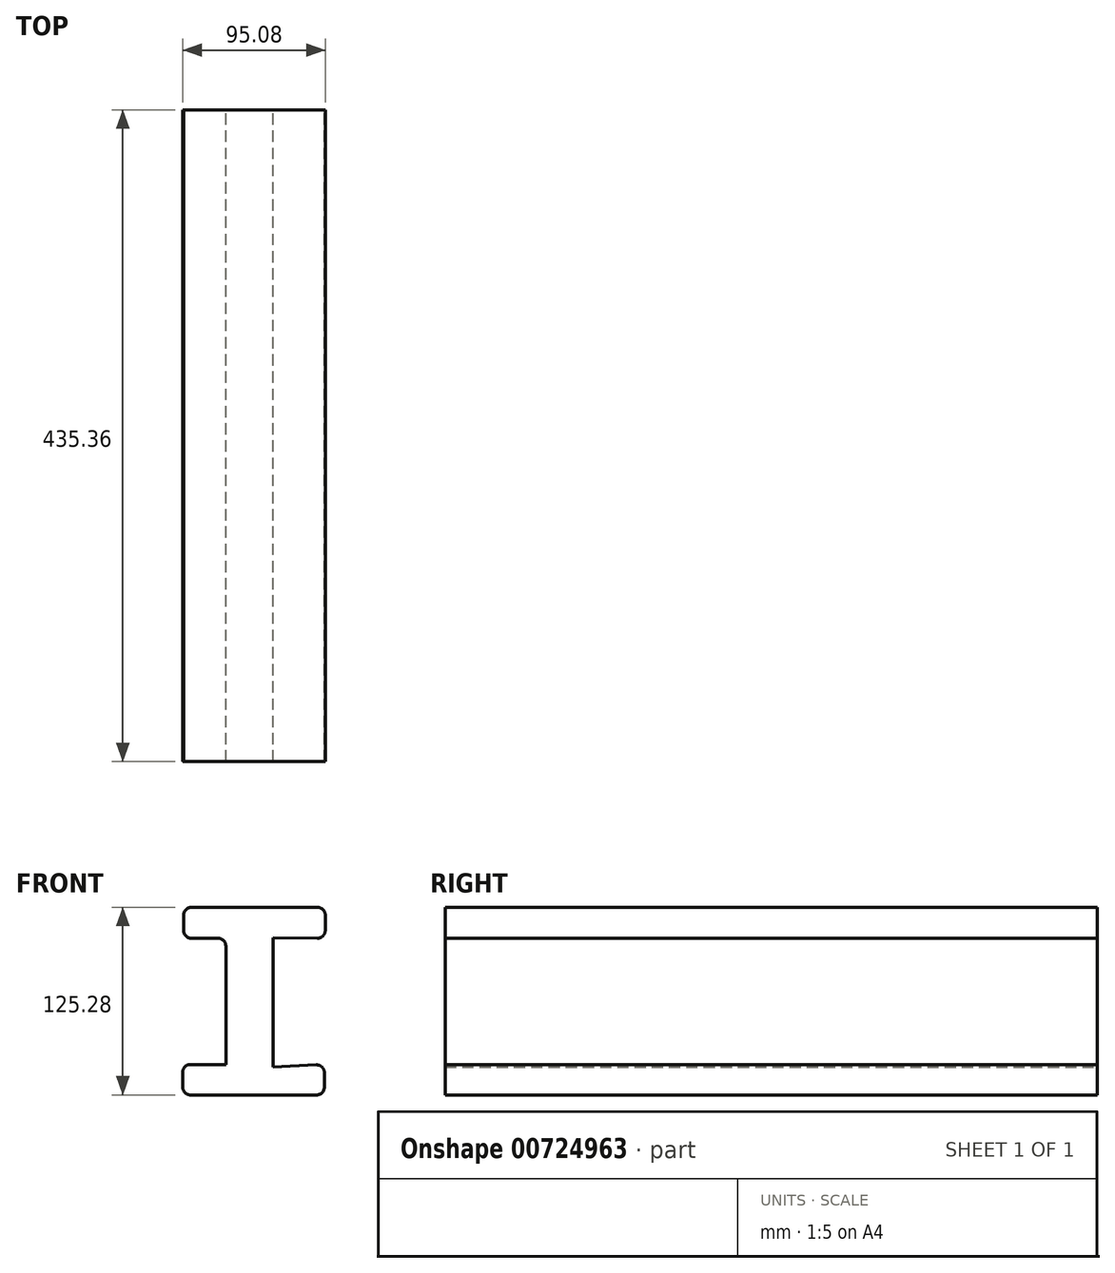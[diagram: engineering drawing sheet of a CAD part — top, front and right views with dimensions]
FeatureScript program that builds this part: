
annotation { "Feature Type Name" : "Feature", "Feature Type Description" : "" }
export const myFeature = defineFeature(function(context is Context, id is Id, definition is map)
    precondition{}
    {
        {
            var Q0;
            Q0=qCreatedBy(makeId("Front.planeOp"),FACE);
            var sketch = newSketch(context, id + "F0", { "sketchPlane" : qUnion([Q0])});
            skLineSegment(sketch, "E0", {"start": v(-18.09, 39.47) * mm, "end": v(-18.09, -44.85) * mm});
            skLineSegment(sketch, "E1", {"start": v(13.6, 39.77) * mm, "end": v(13.6, -46.65) * mm});
            skLineSegment(sketch, "E2", {"start": v(-18.09, 39.47) * mm, "end": v(-46.2, 39.47) * mm});
            skLineSegment(sketch, "E3", {"start": v(-46.2, 39.47) * mm, "end": v(-46.2, 60.1) * mm});
            skLineSegment(sketch, "E4", {"start": v(-46.2, 60.1) * mm, "end": v(48.29, 60.1) * mm});
            skLineSegment(sketch, "E5", {"start": v(48.29, 60.1) * mm, "end": v(48.29, 39.47) * mm});
            skLineSegment(sketch, "E6", {"start": v(48.29, 39.47) * mm, "end": v(13.6, 39.77) * mm});
            skLineSegment(sketch, "E7", {"start": v(-18.09, -44.85) * mm, "end": v(-46.8, -44.85) * mm});
            skLineSegment(sketch, "E8", {"start": v(-46.8, -44.85) * mm, "end": v(-46.8, -65.18) * mm});
            skLineSegment(sketch, "E9", {"start": v(-46.8, -65.18) * mm, "end": v(47.7, -65.18) * mm});
            skLineSegment(sketch, "E10", {"start": v(47.7, -65.18) * mm, "end": v(47.7, -44.85) * mm});
            skLineSegment(sketch, "E11", {"start": v(47.7, -44.85) * mm, "end": v(13.6, -46.65) * mm});
            skSolve(sketch);
        }
        {
            var Q0;
            Q0=makeQuery(id+"F0.imprint","IMPRINT",FACE,{"disambiguationData":[TD([[makeQuery(id+"F0.imprint","IMPRINT",EDGE,{"derivedFrom":sQuery(id+"F0.wireOp",EDGE,"E0")}),1.0]])]});
            extrude(context, id + "F1", {"entities" : qUnion([Q0]), "depth" : 76.2 * mm, "offsetDistance" : 25.4 * mm});
        }
        {
            var Q0;
            Q0=makeQuery(id+"F1.opExtrude","CAP_FACE",FACE,{"disambiguationData":[OSD([sQuery(id+"F0.wireOp",EDGE,"E0"),sQuery(id+"F0.wireOp",EDGE,"E1"),sQuery(id+"F0.wireOp",EDGE,"E2"),sQuery(id+"F0.wireOp",EDGE,"E3"),sQuery(id+"F0.wireOp",EDGE,"E4"),sQuery(id+"F0.wireOp",EDGE,"E5"),sQuery(id+"F0.wireOp",EDGE,"E6"),sQuery(id+"F0.wireOp",EDGE,"E7"),sQuery(id+"F0.wireOp",EDGE,"E8"),sQuery(id+"F0.wireOp",EDGE,"E9"),sQuery(id+"F0.wireOp",EDGE,"E10"),sQuery(id+"F0.wireOp",EDGE,"E11")])],"isStart":true});
            extrude(context, id + "F2", {"entities" : qUnion([Q0]), "operationType" : NewBodyOperationType.ADD, "depth" : 150.11 * mm, "offsetDistance" : 25.4 * mm});
        }
        {
            var Q0;
            Q0=makeQuery(id+"F2.opExtrude","CAP_FACE",FACE,{"disambiguationData":[OSD([sQuery(id+"F0.wireOp",EDGE,"E0"),sQuery(id+"F0.wireOp",EDGE,"E1"),sQuery(id+"F0.wireOp",EDGE,"E2"),sQuery(id+"F0.wireOp",EDGE,"E3"),sQuery(id+"F0.wireOp",EDGE,"E4"),sQuery(id+"F0.wireOp",EDGE,"E5"),sQuery(id+"F0.wireOp",EDGE,"E6"),sQuery(id+"F0.wireOp",EDGE,"E7"),sQuery(id+"F0.wireOp",EDGE,"E8"),sQuery(id+"F0.wireOp",EDGE,"E9"),sQuery(id+"F0.wireOp",EDGE,"E10"),sQuery(id+"F0.wireOp",EDGE,"E11")])],"isStart":false});
            extrude(context, id + "F3", {"entities" : qUnion([Q0]), "operationType" : NewBodyOperationType.ADD, "depth" : 209.04 * mm, "offsetDistance" : 25.4 * mm});
        }
        {
            var Q0;
            {var subQ0=sQuery(id+"F0.wireOp",EDGE,"E3");var subQ1=sQuery(id+"F0.wireOp",EDGE,"E2");Q0=makeQuery(id+"F3.boolean.opBoolean","MERGE",EDGE,{"derivedFrom":[makeQuery(id+"F2.boolean.opBoolean","MERGE",EDGE,{"derivedFrom":[makeQuery(id+"F1.opExtrude","SWEPT_EDGE",EDGE,{"disambiguationData":[OSD([subQ1,subQ0])]}),makeQuery(id+"F2.opExtrude","SWEPT_EDGE",EDGE,{"disambiguationData":[OSD([subQ1,subQ0])]})]}),makeQuery(id+"F3.opExtrude","SWEPT_EDGE",EDGE,{"disambiguationData":[OSD([subQ1,subQ0])]})]});}
            var Q1;
            {var subQ0=sQuery(id+"F0.wireOp",EDGE,"E2");var subQ1=sQuery(id+"F0.wireOp",EDGE,"E0");Q1=makeQuery(id+"F3.boolean.opBoolean","MERGE",EDGE,{"derivedFrom":[makeQuery(id+"F2.boolean.opBoolean","MERGE",EDGE,{"derivedFrom":[makeQuery(id+"F1.opExtrude","SWEPT_EDGE",EDGE,{"disambiguationData":[OSD([subQ1,subQ0])]}),makeQuery(id+"F2.opExtrude","SWEPT_EDGE",EDGE,{"disambiguationData":[OSD([subQ1,subQ0])]})]}),makeQuery(id+"F3.opExtrude","SWEPT_EDGE",EDGE,{"disambiguationData":[OSD([subQ1,subQ0])]})]});}
            var Q2;
            {var subQ0=sQuery(id+"F0.wireOp",EDGE,"E8");var subQ1=sQuery(id+"F0.wireOp",EDGE,"E7");Q2=makeQuery(id+"F3.boolean.opBoolean","MERGE",EDGE,{"derivedFrom":[makeQuery(id+"F2.boolean.opBoolean","MERGE",EDGE,{"derivedFrom":[makeQuery(id+"F1.opExtrude","SWEPT_EDGE",EDGE,{"disambiguationData":[OSD([subQ1,subQ0])]}),makeQuery(id+"F2.opExtrude","SWEPT_EDGE",EDGE,{"disambiguationData":[OSD([subQ1,subQ0])]})]}),makeQuery(id+"F3.opExtrude","SWEPT_EDGE",EDGE,{"disambiguationData":[OSD([subQ1,subQ0])]})]});}
            var Q3;
            {var subQ0=sQuery(id+"F0.wireOp",EDGE,"E9");var subQ1=sQuery(id+"F0.wireOp",EDGE,"E8");Q3=makeQuery(id+"F3.boolean.opBoolean","MERGE",EDGE,{"derivedFrom":[makeQuery(id+"F2.boolean.opBoolean","MERGE",EDGE,{"derivedFrom":[makeQuery(id+"F1.opExtrude","SWEPT_EDGE",EDGE,{"disambiguationData":[OSD([subQ1,subQ0])]}),makeQuery(id+"F2.opExtrude","SWEPT_EDGE",EDGE,{"disambiguationData":[OSD([subQ1,subQ0])]})]}),makeQuery(id+"F3.opExtrude","SWEPT_EDGE",EDGE,{"disambiguationData":[OSD([subQ1,subQ0])]})]});}
            var Q4;
            {var subQ0=sQuery(id+"F0.wireOp",EDGE,"E10");var subQ1=sQuery(id+"F0.wireOp",EDGE,"E9");Q4=makeQuery(id+"F3.boolean.opBoolean","MERGE",EDGE,{"derivedFrom":[makeQuery(id+"F2.boolean.opBoolean","MERGE",EDGE,{"derivedFrom":[makeQuery(id+"F1.opExtrude","SWEPT_EDGE",EDGE,{"disambiguationData":[OSD([subQ1,subQ0])]}),makeQuery(id+"F2.opExtrude","SWEPT_EDGE",EDGE,{"disambiguationData":[OSD([subQ1,subQ0])]})]}),makeQuery(id+"F3.opExtrude","SWEPT_EDGE",EDGE,{"disambiguationData":[OSD([subQ1,subQ0])]})]});}
            var Q5;
            {var subQ0=sQuery(id+"F0.wireOp",EDGE,"E11");var subQ1=sQuery(id+"F0.wireOp",EDGE,"E10");Q5=makeQuery(id+"F3.boolean.opBoolean","MERGE",EDGE,{"derivedFrom":[makeQuery(id+"F2.boolean.opBoolean","MERGE",EDGE,{"derivedFrom":[makeQuery(id+"F1.opExtrude","SWEPT_EDGE",EDGE,{"disambiguationData":[OSD([subQ1,subQ0])]}),makeQuery(id+"F2.opExtrude","SWEPT_EDGE",EDGE,{"disambiguationData":[OSD([subQ1,subQ0])]})]}),makeQuery(id+"F3.opExtrude","SWEPT_EDGE",EDGE,{"disambiguationData":[OSD([subQ1,subQ0])]})]});}
            var Q6;
            {var subQ0=sQuery(id+"F0.wireOp",EDGE,"E6");var subQ1=sQuery(id+"F0.wireOp",EDGE,"E5");Q6=makeQuery(id+"F3.boolean.opBoolean","MERGE",EDGE,{"derivedFrom":[makeQuery(id+"F2.boolean.opBoolean","MERGE",EDGE,{"derivedFrom":[makeQuery(id+"F1.opExtrude","SWEPT_EDGE",EDGE,{"disambiguationData":[OSD([subQ1,subQ0])]}),makeQuery(id+"F2.opExtrude","SWEPT_EDGE",EDGE,{"disambiguationData":[OSD([subQ1,subQ0])]})]}),makeQuery(id+"F3.opExtrude","SWEPT_EDGE",EDGE,{"disambiguationData":[OSD([subQ1,subQ0])]})]});}
            var Q7;
            {var subQ0=sQuery(id+"F0.wireOp",EDGE,"E5");var subQ1=sQuery(id+"F0.wireOp",EDGE,"E4");Q7=makeQuery(id+"F3.boolean.opBoolean","MERGE",EDGE,{"derivedFrom":[makeQuery(id+"F2.boolean.opBoolean","MERGE",EDGE,{"derivedFrom":[makeQuery(id+"F1.opExtrude","SWEPT_EDGE",EDGE,{"disambiguationData":[OSD([subQ1,subQ0])]}),makeQuery(id+"F2.opExtrude","SWEPT_EDGE",EDGE,{"disambiguationData":[OSD([subQ1,subQ0])]})]}),makeQuery(id+"F3.opExtrude","SWEPT_EDGE",EDGE,{"disambiguationData":[OSD([subQ1,subQ0])]})]});}
            var Q8;
            {var subQ0=sQuery(id+"F0.wireOp",EDGE,"E4");var subQ1=sQuery(id+"F0.wireOp",EDGE,"E3");Q8=makeQuery(id+"F3.boolean.opBoolean","MERGE",EDGE,{"derivedFrom":[makeQuery(id+"F2.boolean.opBoolean","MERGE",EDGE,{"derivedFrom":[makeQuery(id+"F1.opExtrude","SWEPT_EDGE",EDGE,{"disambiguationData":[OSD([subQ1,subQ0])]}),makeQuery(id+"F2.opExtrude","SWEPT_EDGE",EDGE,{"disambiguationData":[OSD([subQ1,subQ0])]})]}),makeQuery(id+"F3.opExtrude","SWEPT_EDGE",EDGE,{"disambiguationData":[OSD([subQ1,subQ0])]})]});}
            fillet(context, id + "F4", {"entities" : qUnion([Q0, Q1, Q2, Q3, Q4, Q5, Q6, Q7, Q8]), "radius" : 5.08 * mm, "tangentPropagation" : true, "allowEdgeOverflow" : false});
        }
    });
